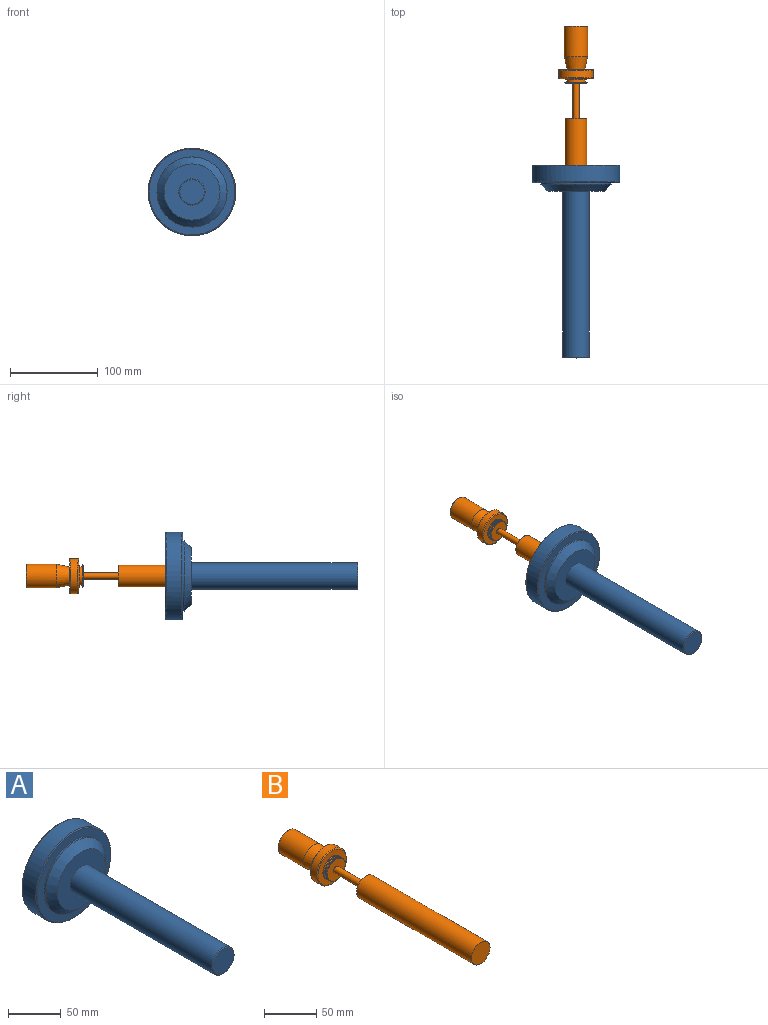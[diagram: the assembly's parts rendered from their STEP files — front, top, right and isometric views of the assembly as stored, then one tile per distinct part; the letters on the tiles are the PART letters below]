
ASSEMBLY  parts=2 mates=1
PART A: 13 faces, bbox 108.2x220x108.2 mm
  f0: cylinder r=15mm len=189mm, axis (0,1,0), area 17812.8mm2, adj f1,f10
  f1: plane 64x64mm, normal (0,-1,0), area 2510.1mm2, adj f0,f11
  f2: cylinder r=40mm len=80mm, axis (0,1,0), area 502.7mm2, adj f3,f11
  f3: plane 98x98mm, normal (0,-1,0), area 2516.4mm2, adj f2,f12
  f4: cylinder r=50mm len=100mm, axis (0,1,0), area 5654.9mm2, adj f9,f12
  f5: plane 98x98mm, normal (0,1,0), area 7048.2mm2, adj f8,f9
  f6: plane 28x28mm, normal (0,-1,0), area 615.8mm2, adj f10
  f7: cone r=0mm half-angle=59deg, axis (0,1,0), area 577.3mm2, adj f8
  f8: cylinder r=12.55mm len=200mm, axis (0,1,0), area 15770.8mm2, adj f5,f7
  f9: torus R=49mm, axis (0,-1,0), area 489.9mm2, adj f4,f5
  f10: torus R=14mm, axis (0,1,0), area 144.5mm2, adj f0,f6
  f11: cone r=40mm half-angle=45deg, axis (0,1,0), area 2559.1mm2, adj f1,f2
  f12: torus R=49mm, axis (0,1,0), area 489.9mm2, adj f3,f4
PART B: 22 faces, bbox 43.3x260.5x43.3 mm
  f0: cylinder r=3.5mm len=40mm, axis (0,-1,0), area 879.6mm2, adj f1,f15
  f1: plane 24.1x24.1mm, normal (0,-1,0), area 417.7mm2, adj f0,f19
  f2: cylinder r=12.55mm len=25.1mm, axis (0,-1,0), area 39.4mm2, adj f19,f20
  f3: plane 24.1x24.1mm, normal (0,1,0), area 106.5mm2, adj f4,f20
  f4: cylinder r=10.55mm len=21.1mm, axis (0,-1,0), area 165.7mm2, adj f3,f5
  f5: plane 24.1x24.1mm, normal (0,-1,0), area 106.5mm2, adj f4,f21
  f6: cylinder r=12.55mm len=25.1mm, axis (0,-1,0), area 78.9mm2, adj f7,f21
  f7: plane 38x38mm, normal (0,-1,0), area 639.3mm2, adj f6,f16
  f8: cylinder r=20mm len=40mm, axis (0,-1,0), area 1005.3mm2, adj f16,f17
  f9: plane 38x38mm, normal (0,1,0), area 820mm2, adj f10,f17
  f10: cone r=10mm half-angle=13.1deg, axis (0,1,0), area 1137.2mm2, adj f9,f11
  f11: cylinder r=13.5mm len=34mm, axis (0,-1,0), area 2884mm2, adj f10,f18
  f12: plane 25x25mm, normal (0,1,0), area 490.9mm2, adj f18
  f13: plane 25x25mm, normal (0,-1,0), area 490.9mm2, adj f14
  f14: cylinder r=12.5mm len=155mm, axis (0,-1,0), area 12173.7mm2, adj f13,f15
  f15: plane 25x25mm, normal (0,1,0), area 452.4mm2, adj f0,f14
  f16: torus R=19mm, axis (0,-1,0), area 193.8mm2, adj f7,f8
  f17: torus R=19mm, axis (0,-1,0), area 193.8mm2, adj f8,f9
  f18: torus R=12.5mm, axis (0,1,0), area 129.7mm2, adj f11,f12
  f19: torus R=12.05mm, axis (0,-1,0), area 61mm2, adj f1,f2
  f20: torus R=12.05mm, axis (0,1,0), area 61mm2, adj f2,f3
  f21: torus R=12.05mm, axis (0,-1,0), area 61mm2, adj f5,f6
PLACE A rot(axis=(0.37,-0.26,0.89),0deg) t=(32.9,-43.75,133.43)mm
PLACE B rot(axis=(0.37,-0.26,0.89),0deg) t=(36.58,12.13,133.43)mm
MATE slider B.f0 <-> A.f7  axis (0,-1,0) through (32.9,19.87,133.43)mm
